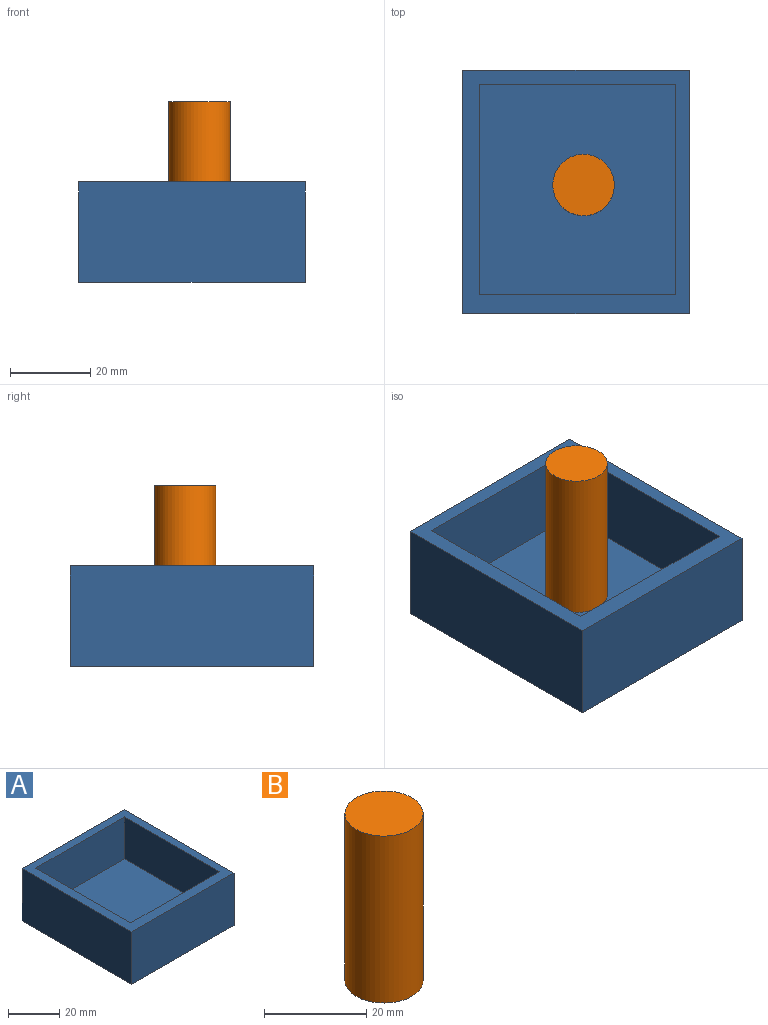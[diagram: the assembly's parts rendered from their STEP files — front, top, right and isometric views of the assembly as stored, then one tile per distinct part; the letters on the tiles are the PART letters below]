
ASSEMBLY  parts=2 mates=1
PART A: 11 faces, bbox 56.3x60.5x25 mm
  f0: plane 60.55x56.27mm, normal (0,0,1), area 852.6mm2, adj f1,f2,f3,f4,f6,f7,f8,f9
  f1: plane 56.27x25mm, normal (0,1,0), area 1406.9mm2, adj f0,f2,f4,f5
  f2: plane 60.55x25mm, normal (-1,0,0), area 1513.7mm2, adj f0,f1,f3,f5
  f3: plane 56.27x25mm, normal (0,-1,0), area 1406.9mm2, adj f0,f2,f4,f5
  f4: plane 60.55x25mm, normal (1,0,0), area 1513.7mm2, adj f0,f1,f3,f5
  f5: plane 60.55x56.27mm, normal (0,0,-1), area 3407.3mm2, adj f1,f2,f3,f4
  f6: plane 48.79x20mm, normal (0,-1,0), area 975.9mm2, adj f0,f7,f9,f10
  f7: plane 52.36x20mm, normal (1,0,0), area 1047.1mm2, adj f0,f6,f8,f10
  f8: plane 48.79x20mm, normal (0,1,0), area 975.9mm2, adj f0,f7,f9,f10
  f9: plane 52.36x20mm, normal (-1,0,0), area 1047.1mm2, adj f0,f6,f8,f10
  f10: plane 52.36x48.79mm, normal (0,0,1), area 2554.7mm2, adj f6,f7,f8,f9
PART B: 3 faces, bbox 15.3x15.3x40 mm
  f0: cylinder r=7.65mm len=40mm, axis (0,0,-1), area 1922.3mm2, adj f1,f2
  f1: plane 15.3x15.3mm, normal (0,0,1), area 183.8mm2, adj f0
  f2: plane 15.3x15.3mm, normal (0,0,-1), area 183.8mm2, adj f0
PLACE A t=(-11.83,-8.71,-5.52)mm fixed
PLACE B rot(axis=(0,0,1),125.9deg) t=(-15.11,-3.46,-0.52)mm
MATE planar A.f10 <-> B.f0  axis (0,0,1) through (-16.63,-4.62,-0.52)mm
